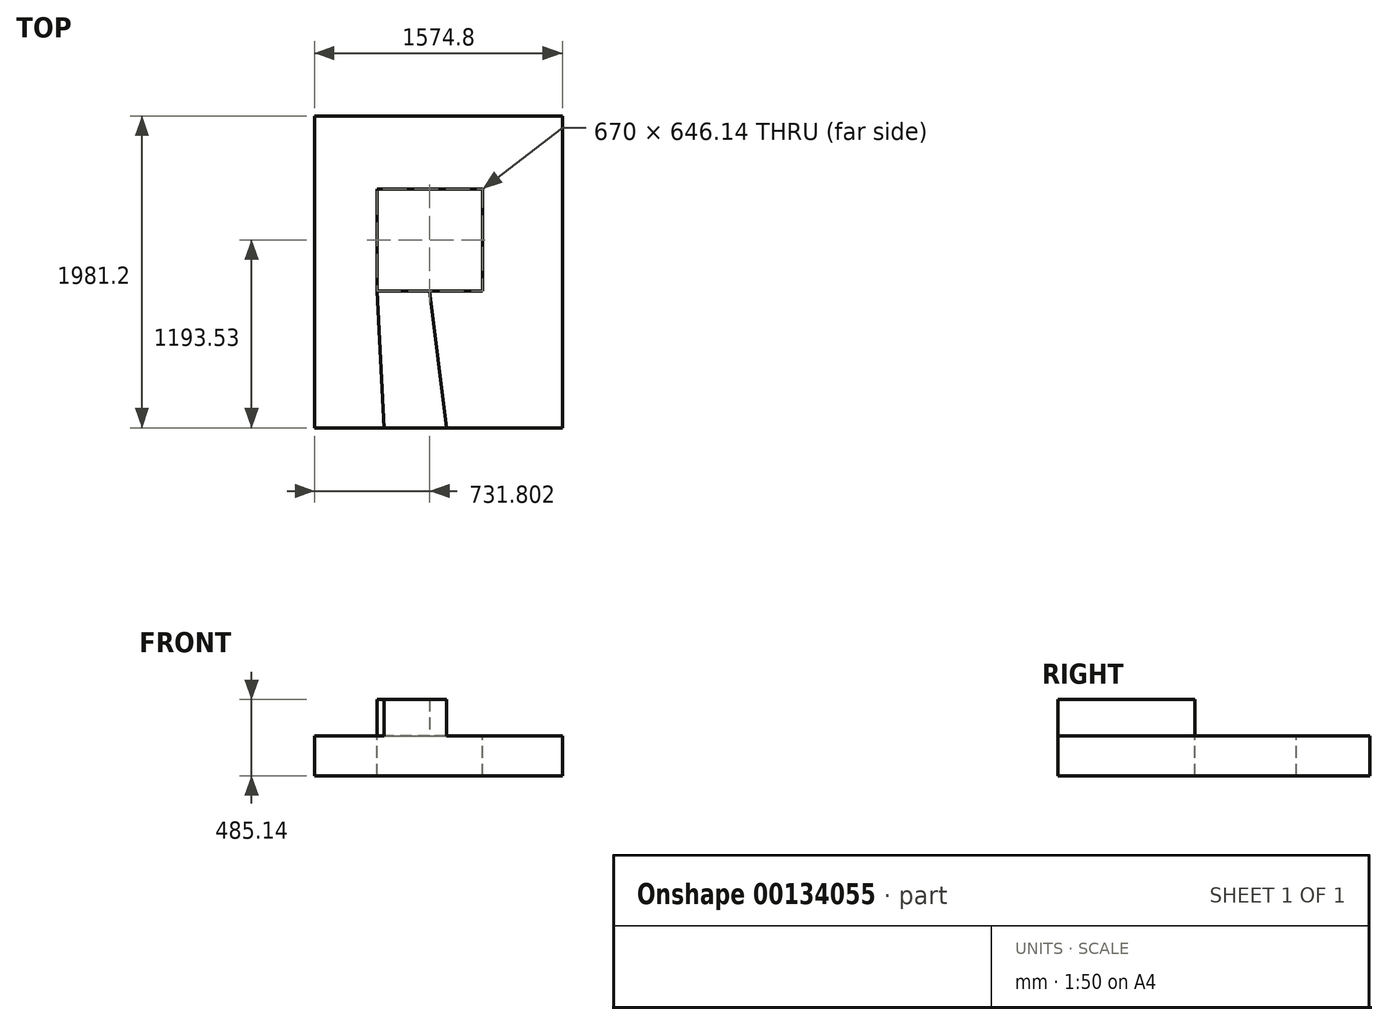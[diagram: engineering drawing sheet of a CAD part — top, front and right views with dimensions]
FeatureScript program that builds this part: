
annotation { "Feature Type Name" : "Feature", "Feature Type Description" : "" }
export const myFeature = defineFeature(function(context is Context, id is Id, definition is map)
    precondition{}
    {
        {
            var Q0;
            Q0=qCreatedBy(makeId("Top.planeOp"),FACE);
            var sketch = newSketch(context, id + "F0", { "sketchPlane" : qUnion([Q0])});
            skLineSegment(sketch, "E0", {"start": v(0, 0) * mm, "end": v(1574.8, 0) * mm});
            skLineSegment(sketch, "E1", {"start": v(0, 0) * mm, "end": v(0, -1981.2) * mm});
            skLineSegment(sketch, "E2", {"start": v(0, -1981.2) * mm, "end": v(1574.8, -1981.2) * mm});
            skLineSegment(sketch, "E3", {"start": v(1574.8, 0) * mm, "end": v(1574.8, -863.6) * mm});
            skLineSegment(sketch, "E4", {"start": v(1574.8, -863.6) * mm, "end": v(1574.8, -1473.2) * mm});
            skLineSegment(sketch, "E5", {"start": v(1574.8, -1473.2) * mm, "end": v(1574.8, -1981.2) * mm});
            skSolve(sketch);
        }
        {
            var Q0;
            Q0=makeQuery(id+"F0.imprint","IMPRINT",FACE,{"disambiguationData":[TD([[makeQuery(id+"F0.imprint","IMPRINT",EDGE,{"derivedFrom":sQuery(id+"F0.wireOp",EDGE,"E0")}),-1.0]])]});
            extrude(context, id + "F1", {"entities" : qUnion([Q0]), "oppositeDirection" : true, "depth" : 254 * mm});
        }
        {
            var Q0;
            Q0=makeQuery(id+"F1.opExtrude","CAP_FACE",FACE,{"disambiguationData":[OSD([sQuery(id+"F0.wireOp",EDGE,"E0"),sQuery(id+"F0.wireOp",EDGE,"E1"),sQuery(id+"F0.wireOp",EDGE,"E2"),sQuery(id+"F0.wireOp",EDGE,"E3"),sQuery(id+"F0.wireOp",EDGE,"E4"),sQuery(id+"F0.wireOp",EDGE,"E5")])],"isStart":true});
            var sketch = newSketch(context, id + "F2", { "sketchPlane" : qUnion([Q0])});
            skLineSegment(sketch, "E6.bottom", {"start": v(396.8, -1110.74) * mm, "end": v(1066.8, -1110.74) * mm});
            skLineSegment(sketch, "E6.top", {"start": v(396.8, -464.6) * mm, "end": v(1066.8, -464.6) * mm});
            skLineSegment(sketch, "E6.left", {"start": v(396.8, -1110.74) * mm, "end": v(396.8, -464.6) * mm});
            skLineSegment(sketch, "E6.right", {"start": v(1066.8, -1110.74) * mm, "end": v(1066.8, -464.6) * mm});
            skPoint(sketch, "E6.middle", {"position": v(731.8, -787.67) * mm});
            skSolve(sketch);
        }
        {
            var Q0;
            Q0 = qSketchRegion(id + "F2", true);
            extrude(context, id + "F3", {"entities" : qUnion([Q0]), "operationType" : NewBodyOperationType.REMOVE, "endBound" : BoundingType.UP_TO_NEXT, "oppositeDirection" : true, "depth" : 25.4 * mm});
        }
        {
            var Q0;
            Q0=makeQuery(id+"F1.opExtrude","CAP_FACE",FACE,{"disambiguationData":[OSD([sQuery(id+"F0.wireOp",EDGE,"E0"),sQuery(id+"F0.wireOp",EDGE,"E1"),sQuery(id+"F0.wireOp",EDGE,"E2"),sQuery(id+"F0.wireOp",EDGE,"E3"),sQuery(id+"F0.wireOp",EDGE,"E4"),sQuery(id+"F0.wireOp",EDGE,"E5")])],"isStart":true});
            var sketch = newSketch(context, id + "F4", { "sketchPlane" : qUnion([Q0])});
            skLineSegment(sketch, "E7", {"start": v(396.8, -1110.74) * mm, "end": v(442.23, -1981.2) * mm});
            skLineSegment(sketch, "E8", {"start": v(442.23, -1981.2) * mm, "end": v(837.07, -1981.2) * mm});
            skLineSegment(sketch, "E9", {"start": v(837.07, -1981.2) * mm, "end": v(731.8, -1110.74) * mm});
            skLineSegment(sketch, "E10", {"start": v(741.53, -1111.26) * mm, "end": v(396.8, -1110.74) * mm});
            skSolve(sketch);
        }
        {
            var Q0;
            Q0 = qSketchRegion(id + "F4", true);
            extrude(context, id + "F5", {"entities" : qUnion([Q0]), "operationType" : NewBodyOperationType.ADD, "depth" : 231.14 * mm, "offsetDistance" : 25.4 * mm});
        }
    });
